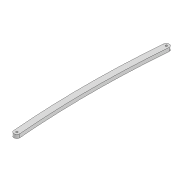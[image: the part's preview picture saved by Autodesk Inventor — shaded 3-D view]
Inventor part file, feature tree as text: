
AUTODESK INVENTOR PART (.ipt)
format: ipt  version: 2022 (Build 260153000, 153)  size: 93,184 bytes
history: native  units: mm
features: extrude x1, sketch x1
ambient origin geometry x8: Origin, YZ Plane, XZ Plane, XY Plane, X Axis, Y Axis, Z Axis, Center Point
bodies: Solid1 (feature_tree)
feature tree (2):
  extrude  "Extrusion1"  Depth=1500.0mm
  sketch  "Sketch1"  dims[d0=3.3mm d1=3.3mm d2=10.0mm d3=253.429mm d6=6.0mm d7=0.0mm d16=1500.0mm d17=1500.0mm]
